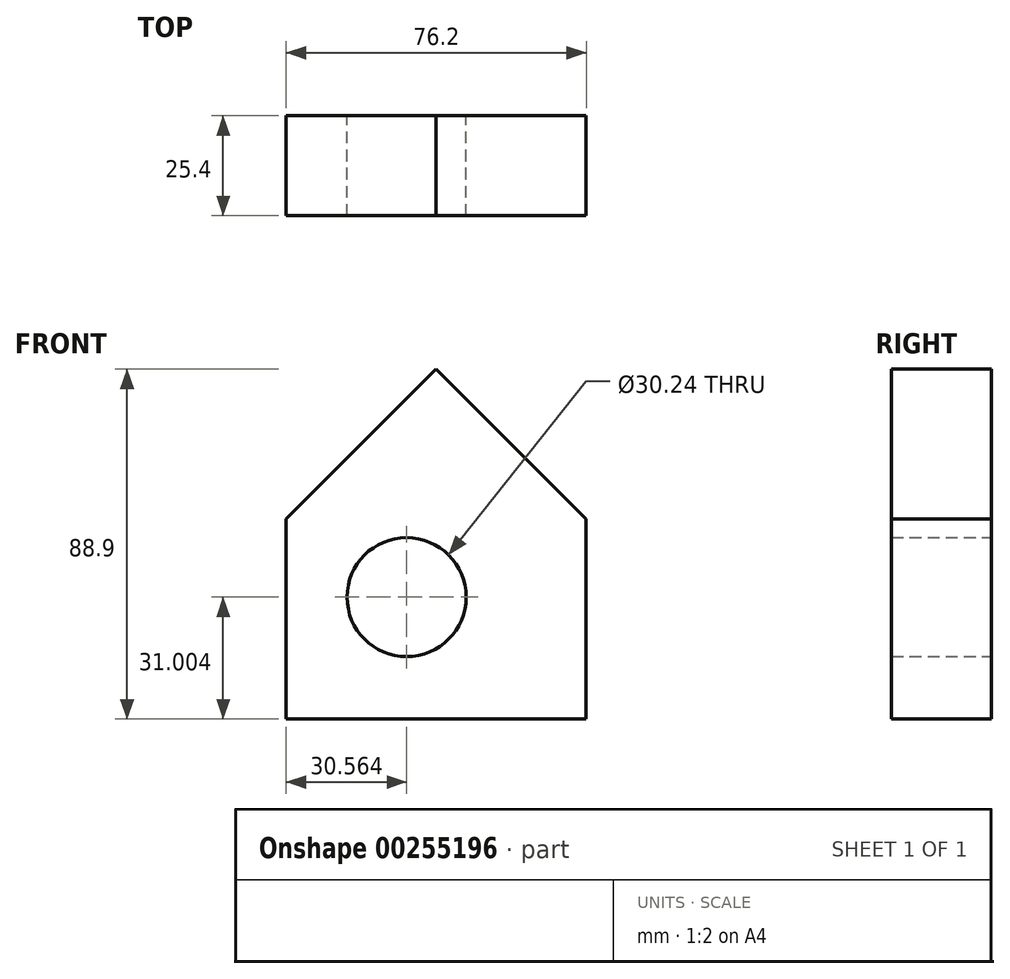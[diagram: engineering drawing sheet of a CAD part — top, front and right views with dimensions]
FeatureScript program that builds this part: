
annotation { "Feature Type Name" : "Feature", "Feature Type Description" : "" }
export const myFeature = defineFeature(function(context is Context, id is Id, definition is map)
    precondition{}
    {
        {
            var Q0;
            Q0=qCreatedBy(makeId("Front.planeOp"),FACE);
            var sketch = newSketch(context, id + "F0", { "sketchPlane" : qUnion([Q0])});
            skLineSegment(sketch, "E0.top", {"start": v(2.76, -15.86) * mm, "end": v(-73.44, -15.86) * mm});
            skLineSegment(sketch, "E0.left", {"start": v(2.76, 34.94) * mm, "end": v(2.76, -15.86) * mm});
            skLineSegment(sketch, "E0.right", {"start": v(-73.44, 34.94) * mm, "end": v(-73.44, -15.86) * mm});
            skLineSegment(sketch, "E1", {"start": v(-73.44, 34.94) * mm, "end": v(-35.34, 73.04) * mm});
            skLineSegment(sketch, "E2", {"start": v(-35.34, 73.04) * mm, "end": v(2.76, 34.94) * mm});
            skCircle(sketch, "E3", {"center": v(-42.88, 15.14) * mm, "radius": 15.12 * mm});
            skSolve(sketch);
        }
        {
            var Q0;
            Q0=makeQuery(id+"F0.imprint","IMPRINT",FACE,{"disambiguationData":[TD([[makeQuery(id+"F0.imprint","IMPRINT",EDGE,{"derivedFrom":sQuery(id+"F0.wireOp",EDGE,"E0.top")}),-1.0]])]});
            extrude(context, id + "F1", {"entities" : qUnion([Q0]), "depth" : 25.4 * mm});
        }
    });
